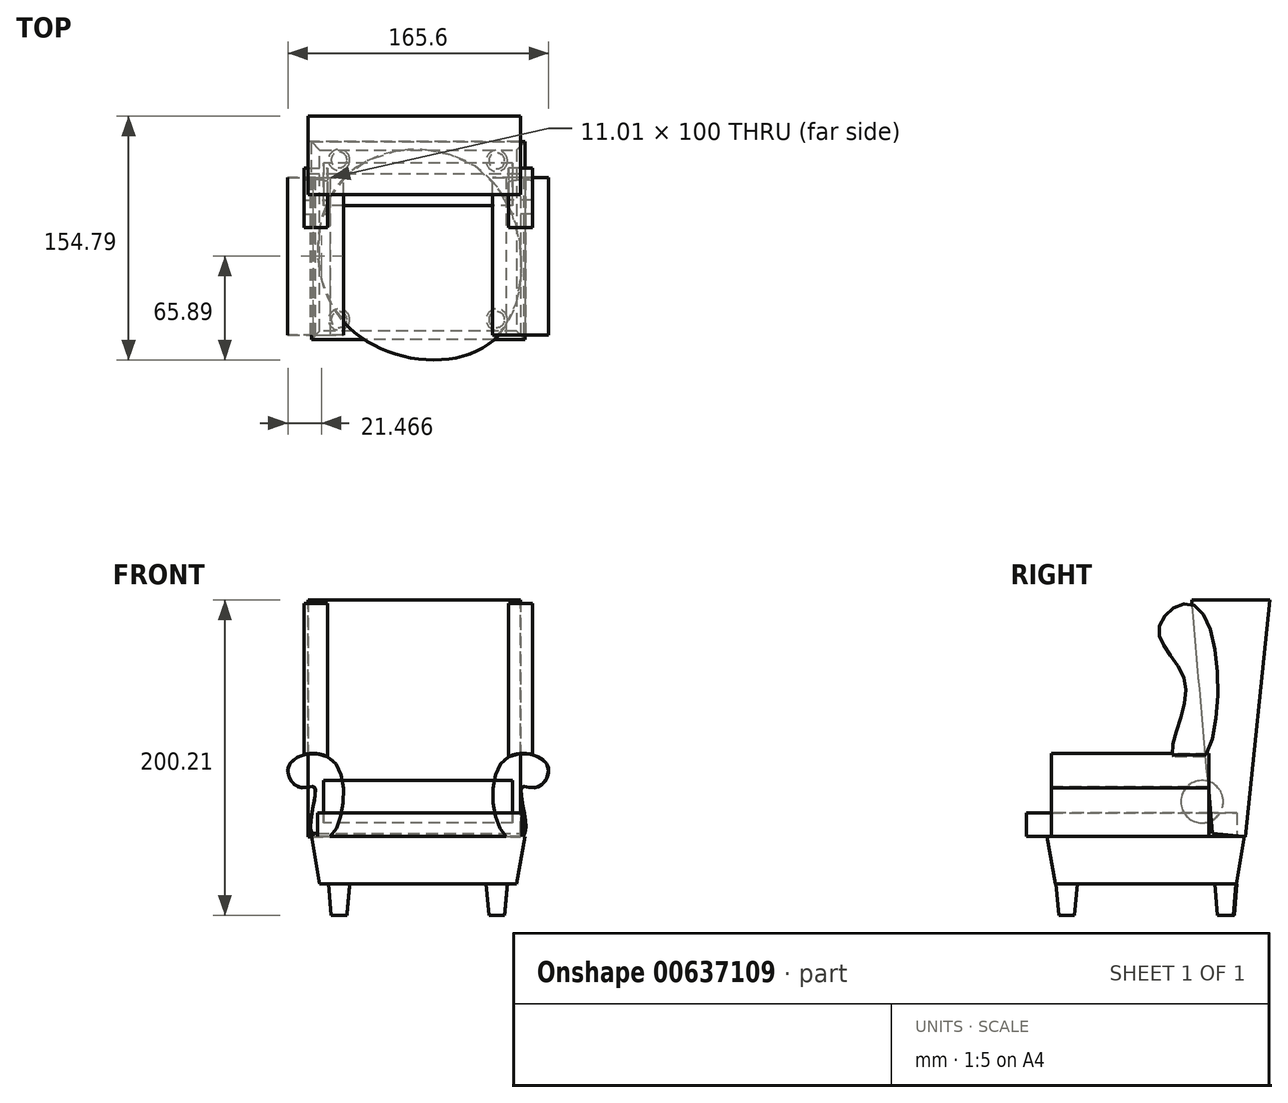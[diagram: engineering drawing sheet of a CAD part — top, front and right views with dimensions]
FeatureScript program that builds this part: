
annotation { "Feature Type Name" : "Feature", "Feature Type Description" : "" }
export const myFeature = defineFeature(function(context is Context, id is Id, definition is map)
    precondition{}
    {
        {
            var Q0;
            Q0=qCreatedBy(makeId("Top.planeOp"),FACE);
            var sketch = newSketch(context, id + "F0", { "sketchPlane" : qUnion([Q0])});
            skCircle(sketch, "E0", {"center": v(-50.24, 51.19) * mm, "radius": 5 * mm});
            skCircle(sketch, "E1", {"center": v(49.93, 50.56) * mm, "radius": 5 * mm});
            skCircle(sketch, "E2", {"center": v(-50.24, -50.24) * mm, "radius": 5 * mm});
            skCircle(sketch, "E3", {"center": v(49.93, -50.24) * mm, "radius": 5 * mm});
            skSolve(sketch);
        }
        {
            var Q0;
            Q0 = qSketchRegion(id + "F0", true);
            extrude(context, id + "F1", {"entities" : qUnion([Q0]), "depth" : 20 * mm, "offsetDistance" : 25 * mm, "hasDraft" : true, "draftAngle" : 5 * degree});
        }
        {
            var Q0;
            Q0=qCreatedBy(makeId("Top.planeOp"),FACE);
            cPlane(context, id + "F2", {"entities" : qUnion([Q0]), "cplaneType" : CPlaneType.OFFSET, "offset" : 20 * mm, "width" : 150 * mm, "height" : 150 * mm});
        }
        {
            var Q0;
            Q0=qCreatedBy(id+"F2.planeOp",FACE);
            var sketch = newSketch(context, id + "F3", { "sketchPlane" : qUnion([Q0])});
            skLineSegment(sketch, "E4.bottom", {"start": v(62.5, -57.5) * mm, "end": v(-62.5, -57.5) * mm});
            skLineSegment(sketch, "E4.top", {"start": v(62.5, 57.5) * mm, "end": v(-62.5, 57.5) * mm});
            skLineSegment(sketch, "E4.left", {"start": v(62.5, -57.5) * mm, "end": v(62.5, 57.5) * mm});
            skLineSegment(sketch, "E4.right", {"start": v(-62.5, -57.5) * mm, "end": v(-62.5, 57.5) * mm});
            skPoint(sketch, "E4.middle", {"position": v(0, 0) * mm});
            skSolve(sketch);
        }
        {
            var Q0;
            Q0 = qSketchRegion(id + "F3", true);
            extrude(context, id + "F4", {"entities" : qUnion([Q0]), "depth" : 30 * mm, "offsetDistance" : 25 * mm, "hasDraft" : true, "draftAngle" : 10 * degree});
        }
        {
            var Q0;
            Q0=qCreatedBy(id+"F2.planeOp",FACE);
            cPlane(context, id + "F5", {"entities" : qUnion([Q0]), "cplaneType" : CPlaneType.OFFSET, "offset" : 30 * mm, "width" : 150 * mm, "height" : 150 * mm});
        }
        {
            var Q0;
            Q0=qCreatedBy(makeId("Right.planeOp"),FACE);
            cPlane(context, id + "F6", {"entities" : qUnion([Q0]), "cplaneType" : CPlaneType.OFFSET, "offset" : 65 * mm, "width" : 150 * mm, "height" : 150 * mm});
        }
        {
            var Q0;
            Q0=qCreatedBy(makeId("Front.planeOp"),FACE);
            cPlane(context, id + "F7", {"entities" : qUnion([Q0]), "cplaneType" : CPlaneType.OFFSET, "offset" : 60 * mm, "width" : 150 * mm, "height" : 150 * mm});
        }
        {
            var Q0;
            Q0=qCreatedBy(id+"F7.planeOp",FACE);
            var sketch = newSketch(context, id + "F8", { "sketchPlane" : qUnion([Q0])});
            skFitSpline(sketch, "E5", {"points": [v(-67.64, 51.55) * mm, v(-65.73, 81.19) * mm, v(-75.29, 81.19) * mm, v(-81.98, 95.53) * mm, v(-54.25, 98.4) * mm, v(-55.2, 50.6) * mm, v(-67.64, 51.55) * mm]});
            skSolve(sketch);
        }
        {
            var Q0;
            Q0=makeQuery(id+"F8.imprint","IMPRINT",FACE,{"disambiguationData":[TD([[makeQuery(id+"F8.imprint","IMPRINT",EDGE,{"derivedFrom":sQuery(id+"F8.wireOp",EDGE,"E5")}),-1.0]])]});
            extrude(context, id + "F9", {"entities" : qUnion([Q0]), "operationType" : NewBodyOperationType.ADD, "oppositeDirection" : true, "depth" : 100 * mm, "offsetDistance" : 25 * mm});
        }
        {
            var Q0;
            Q0=makeQuery(id+"F4.opExtrude","SWEPT_BODY",BODY,{"disambiguationData":[OSD([sQuery(id+"F3.wireOp",EDGE,"E4.bottom"),sQuery(id+"F3.wireOp",EDGE,"E4.top"),sQuery(id+"F3.wireOp",EDGE,"E4.left"),sQuery(id+"F3.wireOp",EDGE,"E4.right")])]});
            var Q1;
            Q1=qCreatedBy(makeId("Right.planeOp"),FACE);
            mirror(context, id + "F10", {"entities" : qUnion([Q0]), "mirrorPlane" : qUnion([Q1])});
        }
        {
            var Q0;
            Q0=qCreatedBy(id+"F6.planeOp",FACE);
            var sketch = newSketch(context, id + "F11", { "sketchPlane" : qUnion([Q0])});
            skFitSpline(sketch, "E6", {"points": [v(17.46, 99.55) * mm, v(25.3, 146.61) * mm, v(8.31, 181.9) * mm, v(31.84, 196.29) * mm, v(35.77, 98.24) * mm, v(17.46, 99.55) * mm]});
            skSolve(sketch);
        }
        {
            var Q0;
            Q0 = qSketchRegion(id + "F11", true);
            extrude(context, id + "F12", {"entities" : qUnion([Q0]), "operationType" : NewBodyOperationType.ADD, "endBound" : BoundingType.SYMMETRIC, "depth" : 15 * mm, "offsetDistance" : 25 * mm});
        }
        {
            var Q0;
            Q0=makeQuery(id+"F10.opPattern","COPY",BODY,{"derivedFrom":makeQuery(id+"F4.opExtrude","SWEPT_BODY",BODY,{"disambiguationData":[OSD([sQuery(id+"F3.wireOp",EDGE,"E4.bottom"),sQuery(id+"F3.wireOp",EDGE,"E4.top"),sQuery(id+"F3.wireOp",EDGE,"E4.left"),sQuery(id+"F3.wireOp",EDGE,"E4.right")])]}),"instanceName":"1"});
            var Q1;
            Q1=qCreatedBy(makeId("Right.planeOp"),FACE);
            mirror(context, id + "F13", {"entities" : qUnion([Q0]), "mirrorPlane" : qUnion([Q1])});
        }
        {
            var Q0;
            Q0=qCreatedBy(id+"F6.planeOp",FACE);
            var sketch = newSketch(context, id + "F14", { "sketchPlane" : qUnion([Q0])});
            skLineSegment(sketch, "E7", {"start": v(29.23, 200.2) * mm, "end": v(78.9, 200.2) * mm});
            skLineSegment(sketch, "E8", {"start": v(78.9, 200.2) * mm, "end": v(63.22, 49.87) * mm});
            skLineSegment(sketch, "E9", {"start": v(63.22, 49.87) * mm, "end": v(42.4, 52.05) * mm});
            skLineSegment(sketch, "E10", {"start": v(42.4, 52.05) * mm, "end": v(29.23, 200.2) * mm});
            skSolve(sketch);
        }
        {
            var Q0;
            Q0 = qSketchRegion(id + "F14", true);
            extrude(context, id + "F15", {"entities" : qUnion([Q0]), "oppositeDirection" : true, "depth" : 135 * mm, "offsetDistance" : 25 * mm});
        }
        {
            var Q0;
            Q0=qCreatedBy(id+"F5.planeOp",FACE);
            var sketch = newSketch(context, id + "F16", { "sketchPlane" : qUnion([Q0])});
            skFitSpline(sketch, "E11", {"points": [v(-45.78, 41.2) * mm, v(-47.45, -51.8) * mm, v(48.85, -62.4) * mm, v(45.57, 39.38) * mm, v(-45.78, 41.2) * mm]});
            skSolve(sketch);
        }
        {
            var Q0;
            Q0 = qSketchRegion(id + "F16", true);
            extrude(context, id + "F17", {"entities" : qUnion([Q0]), "depth" : 15 * mm, "offsetDistance" : 25 * mm});
        }
        {
            var Q0;
            Q0=qCreatedBy(makeId("Right.planeOp"),FACE);
            var sketch = newSketch(context, id + "F18", { "sketchPlane" : qUnion([Q0])});
            skCircle(sketch, "E12", {"center": v(35.77, 72.1) * mm, "radius": 13.46 * mm});
            skSolve(sketch);
        }
        {
            var Q0;
            Q0 = qSketchRegion(id + "F18", true);
            extrude(context, id + "F19", {"entities" : qUnion([Q0]), "endBound" : BoundingType.SYMMETRIC, "depth" : 120 * mm, "offsetDistance" : 25 * mm});
        }
    });
